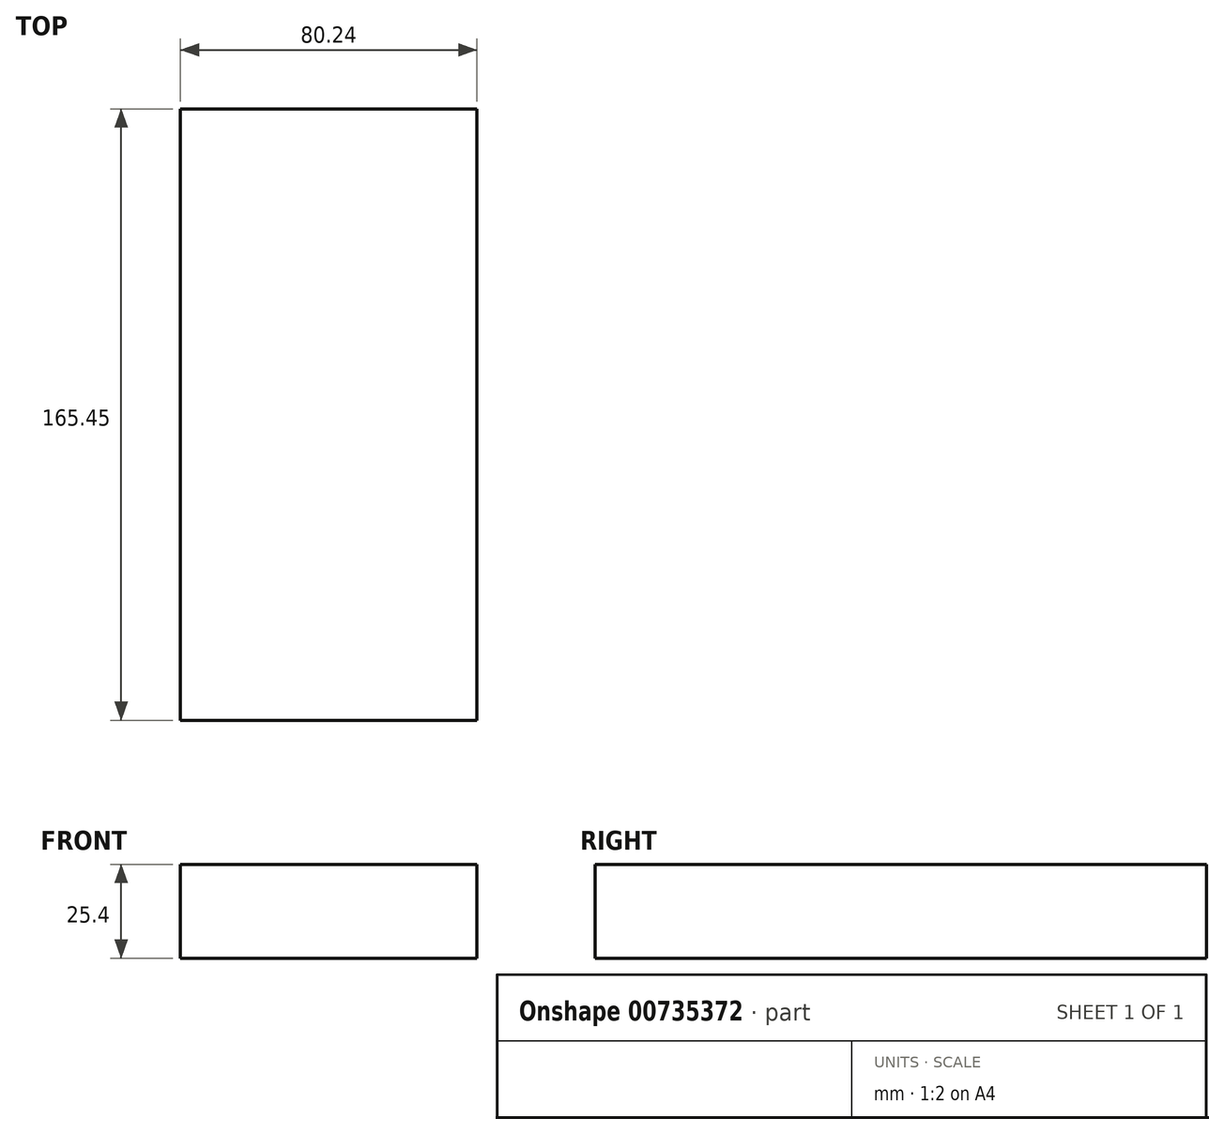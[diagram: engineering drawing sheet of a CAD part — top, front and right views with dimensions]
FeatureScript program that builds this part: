
annotation { "Feature Type Name" : "Feature", "Feature Type Description" : "" }
export const myFeature = defineFeature(function(context is Context, id is Id, definition is map)
    precondition{}
    {
        {
            var Q0;
            Q0=qCreatedBy(makeId("Top.planeOp"),FACE);
            var sketch = newSketch(context, id + "F0", { "sketchPlane" : qUnion([Q0])});
            skLineSegment(sketch, "E0.bottom", {"start": v(40.12, -25.83) * mm, "end": v(-40.12, -25.83) * mm});
            skLineSegment(sketch, "E0.top", {"start": v(40.12, 25.83) * mm, "end": v(-40.12, 25.83) * mm});
            skLineSegment(sketch, "E0.left", {"start": v(40.12, -25.83) * mm, "end": v(40.12, 25.83) * mm});
            skLineSegment(sketch, "E0.right", {"start": v(-40.12, -25.83) * mm, "end": v(-40.12, 25.83) * mm});
            skPoint(sketch, "E0.middle", {"position": v(0, 0) * mm});
            skSolve(sketch);
        }
        {
            var Q0;
            Q0=qCreatedBy(makeId("Top.planeOp"),FACE);
            var sketch = newSketch(context, id + "F1", { "sketchPlane" : qUnion([Q0])});
            skCircle(sketch, "E1", {"center": v(0, 0) * mm, "radius": 12.35 * mm});
            skSolve(sketch);
        }
        {
            var Q0;
            Q0=makeQuery(id+"F0.imprint","IMPRINT",FACE,{"disambiguationData":[TD([[makeQuery(id+"F0.imprint","IMPRINT",EDGE,{"derivedFrom":sQuery(id+"F0.wireOp",EDGE,"E0.bottom")}),-1.0]])]});
            extrude(context, id + "F2", {"entities" : qUnion([Q0]), "depth" : 25.4 * mm, "offsetDistance" : 25.4 * mm});
        }
        {
            var Q0;
            Q0=makeQuery(id+"F1.imprint","IMPRINT",FACE,{"disambiguationData":[TD([[makeQuery(id+"F1.imprint","IMPRINT",EDGE,{"derivedFrom":sQuery(id+"F1.wireOp",EDGE,"E1")}),1.0]])]});
            extrude(context, id + "F3", {"entities" : qUnion([Q0]), "operationType" : NewBodyOperationType.ADD, "depth" : 25.4 * mm, "offsetDistance" : 25.4 * mm});
        }
        {
            var Q0;
            Q0=qCreatedBy(makeId("Top.planeOp"),FACE);
            var sketch = newSketch(context, id + "F4", { "sketchPlane" : qUnion([Q0])});
            skCircle(sketch, "E2", {"center": v(0, 0) * mm, "radius": 18.9 * mm});
            skSolve(sketch);
        }
        {
            var Q0;
            Q0=makeQuery(id+"F4.imprint","IMPRINT",FACE,{"disambiguationData":[TD([[makeQuery(id+"F4.imprint","IMPRINT",EDGE,{"derivedFrom":sQuery(id+"F4.wireOp",EDGE,"E2")}),1.0]])]});
            extrude(context, id + "F5", {"entities" : qUnion([Q0]), "operationType" : NewBodyOperationType.ADD, "depth" : 25.4 * mm, "offsetDistance" : 25.4 * mm});
        }
        {
            var Q0;
            Q0=makeQuery(id+"F2.opExtrude","SWEPT_FACE",FACE,{"disambiguationData":[OSD([sQuery(id+"F0.wireOp",EDGE,"E0.top")])]});
            extrude(context, id + "F6", {"entities" : qUnion([Q0]), "operationType" : NewBodyOperationType.ADD, "depth" : 113.8 * mm, "offsetDistance" : 25.4 * mm});
        }
    });
